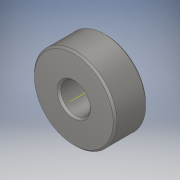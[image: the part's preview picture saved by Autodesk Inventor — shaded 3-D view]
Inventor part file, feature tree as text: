
AUTODESK INVENTOR PART (.ipt)
format: ipt  version: 2019.4 (Build 234330000, 330)  size: 121,856 bytes
history: native  units: in
note: dims shown in document units (in); Inventor stores cm internally (conversion verified against a paired STEP export)
features: plane x2, extrude x1, chamfer x1, sketch x1
ambient origin geometry x8: Origin, YZ Plane, XZ Plane, XY Plane, X Axis, Y Axis, Z Axis, Center Point
bodies: Solid1 (feature_tree)
feature tree (5):
  extrude  "Extrusion1"  Depth=0.3438in TaperAngle=45.0deg
  chamfer  "Chamfer1"  Distance=0.3125in
  plane  "Work Plane1"
  plane  "Work Plane2"
  sketch  "Sketch1"  dims[d2=0.3438in d3=0.0in d4=0.02in d5=0.125in d6=45.0deg d7=0.3125in d8=0.875in]
